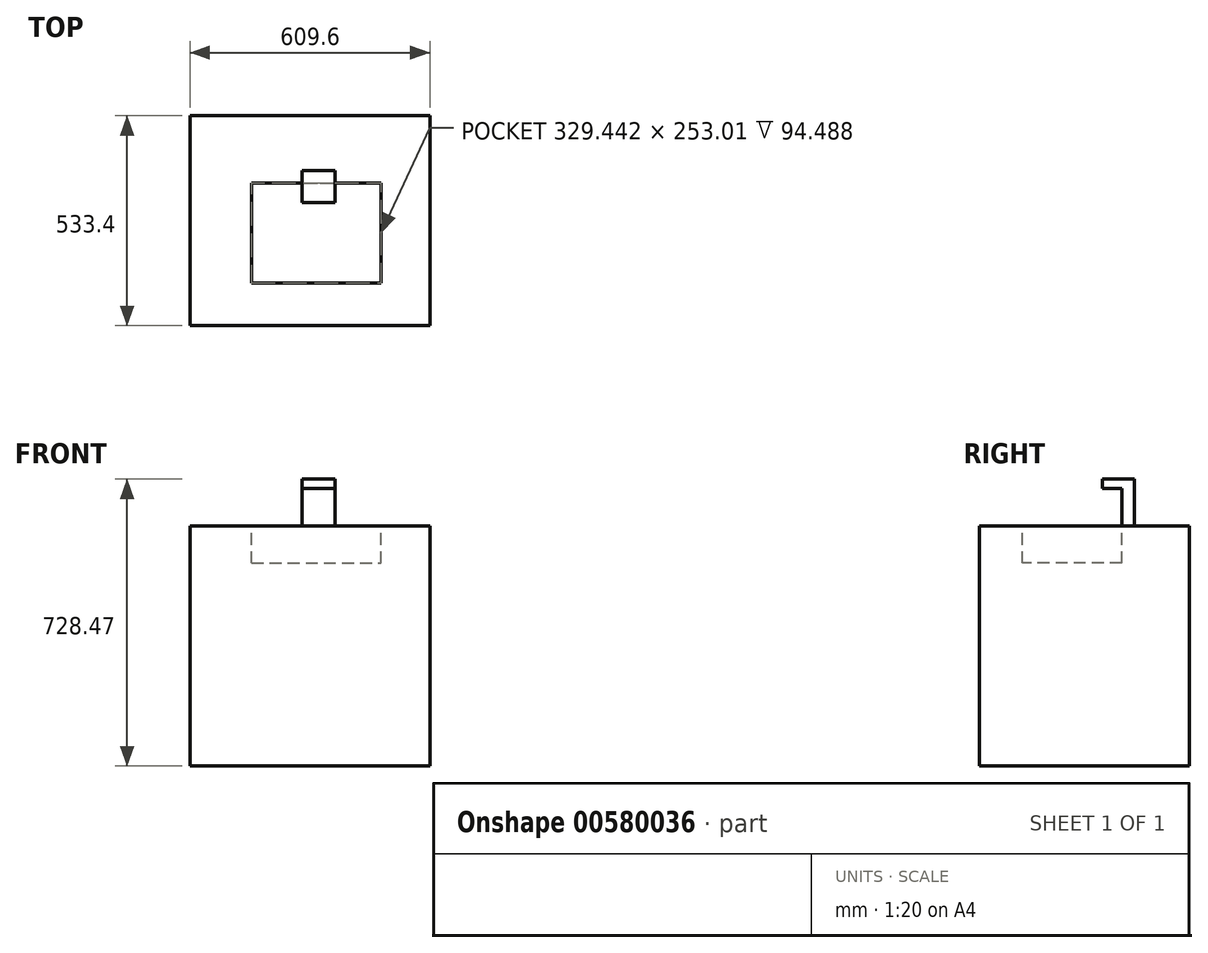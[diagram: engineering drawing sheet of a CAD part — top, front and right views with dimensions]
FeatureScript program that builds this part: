
annotation { "Feature Type Name" : "Feature", "Feature Type Description" : "" }
export const myFeature = defineFeature(function(context is Context, id is Id, definition is map)
    precondition{}
    {
        {
            var Q0;
            Q0=qCreatedBy(makeId("Top.planeOp"),FACE);
            var sketch = newSketch(context, id + "F0", { "sketchPlane" : qUnion([Q0])});
            skLineSegment(sketch, "E0.bottom", {"start": v(-309.67, 270.88) * mm, "end": v(299.93, 270.88) * mm});
            skLineSegment(sketch, "E0.top", {"start": v(-309.67, -262.52) * mm, "end": v(299.93, -262.52) * mm});
            skLineSegment(sketch, "E0.left", {"start": v(-309.67, 270.88) * mm, "end": v(-309.67, -262.52) * mm});
            skLineSegment(sketch, "E0.right", {"start": v(299.93, 270.88) * mm, "end": v(299.93, -262.52) * mm});
            skSolve(sketch);
        }
        {
            var Q0;
            Q0 = qSketchRegion(id + "F0", true);
            extrude(context, id + "F1", {"entities" : qUnion([Q0]), "depth" : 609.6 * mm, "offsetDistance" : 30.48 * mm});
        }
        {
            var Q0;
            Q0=makeQuery(id+"F1.opExtrude","CAP_FACE",FACE,{"disambiguationData":[OSD([sQuery(id+"F0.wireOp",EDGE,"E0.bottom"),sQuery(id+"F0.wireOp",EDGE,"E0.top"),sQuery(id+"F0.wireOp",EDGE,"E0.left"),sQuery(id+"F0.wireOp",EDGE,"E0.right")])],"isStart":false});
            var sketch = newSketch(context, id + "F2", { "sketchPlane" : qUnion([Q0])});
            skLineSegment(sketch, "E1.bottom", {"start": v(-153.41, 99.18) * mm, "end": v(176.03, 99.18) * mm});
            skLineSegment(sketch, "E1.top", {"start": v(-153.41, -153.83) * mm, "end": v(176.03, -153.83) * mm});
            skLineSegment(sketch, "E1.left", {"start": v(-153.41, 99.18) * mm, "end": v(-153.41, -153.83) * mm});
            skLineSegment(sketch, "E1.right", {"start": v(176.03, 99.18) * mm, "end": v(176.03, -153.83) * mm});
            skSolve(sketch);
        }
        {
            var Q0;
            Q0 = qSketchRegion(id + "F2", true);
            extrude(context, id + "F3", {"entities" : qUnion([Q0]), "operationType" : NewBodyOperationType.REMOVE, "oppositeDirection" : true, "depth" : 94.49 * mm, "offsetDistance" : 30.48 * mm});
        }
        {
            var Q0;
            Q0=makeQuery(id+"F1.opExtrude","CAP_FACE",FACE,{"disambiguationData":[OSD([sQuery(id+"F0.wireOp",EDGE,"E0.bottom"),sQuery(id+"F0.wireOp",EDGE,"E0.top"),sQuery(id+"F0.wireOp",EDGE,"E0.left"),sQuery(id+"F0.wireOp",EDGE,"E0.right")])],"isStart":false});
            var sketch = newSketch(context, id + "F4", { "sketchPlane" : qUnion([Q0])});
            skLineSegment(sketch, "E2.bottom", {"start": v(-25.3, 99.18) * mm, "end": v(58.75, 99.18) * mm});
            skLineSegment(sketch, "E2.top", {"start": v(-25.3, 130.9) * mm, "end": v(58.75, 130.9) * mm});
            skLineSegment(sketch, "E2.left", {"start": v(-25.3, 99.18) * mm, "end": v(-25.3, 130.9) * mm});
            skLineSegment(sketch, "E2.right", {"start": v(58.75, 99.18) * mm, "end": v(58.75, 130.9) * mm});
            skSolve(sketch);
        }
        {
            var Q0;
            Q0 = qSketchRegion(id + "F4", true);
            extrude(context, id + "F5", {"entities" : qUnion([Q0]), "operationType" : NewBodyOperationType.ADD, "depth" : 118.87 * mm, "offsetDistance" : 30.48 * mm});
        }
        {
            var Q0;
            Q0=makeQuery(id+"F5.boolean.opBoolean","MERGE",FACE,{"derivedFrom":[makeQuery(id+"F3.boolean.opBoolean","COPY",FACE,{"derivedFrom":makeQuery(id+"F3.opExtrude","SWEPT_FACE",FACE,{"disambiguationData":[OSD([sQuery(id+"F2.wireOp",EDGE,"E1.bottom")])]})}),makeQuery(id+"F5.opExtrude","SWEPT_FACE",FACE,{"disambiguationData":[OSD([sQuery(id+"F4.wireOp",EDGE,"E2.bottom")])]})]});
            var sketch = newSketch(context, id + "F6", { "sketchPlane" : qUnion([Q0])});
            skLineSegment(sketch, "E3.bottom", {"start": v(-25.3, 728.47) * mm, "end": v(58.75, 728.47) * mm});
            skLineSegment(sketch, "E3.top", {"start": v(-25.3, 705.05) * mm, "end": v(58.75, 705.05) * mm});
            skLineSegment(sketch, "E3.left", {"start": v(-25.3, 728.47) * mm, "end": v(-25.3, 705.05) * mm});
            skLineSegment(sketch, "E3.right", {"start": v(58.75, 728.47) * mm, "end": v(58.75, 705.05) * mm});
            skSolve(sketch);
        }
        {
            var Q0;
            Q0 = qSketchRegion(id + "F6", true);
            extrude(context, id + "F7", {"entities" : qUnion([Q0]), "operationType" : NewBodyOperationType.ADD, "depth" : 48.77 * mm, "offsetDistance" : 30.48 * mm});
        }
    });
